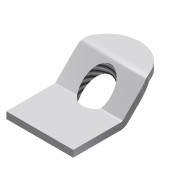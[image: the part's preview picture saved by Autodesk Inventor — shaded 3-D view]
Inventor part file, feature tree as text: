
AUTODESK INVENTOR PART (.ipt)
format: ipt  version: 2015 (Build 190159000, 159)  size: 161,792 bytes
history: native  units: mm
features: sketch x3, sweep x1, fillet x1, hole x1, pattern_linear x1, other x1
ambient origin geometry x8: Origin, YZ Plane, XZ Plane, XY Plane, X Axis, Y Axis, Z Axis, Center Point
bodies: Body1 (feature_tree)
feature tree (8):
  sweep  "Przeciągnięcie1"
  fillet  "Zaokrąglenie1"  Radius=20.594885mm
  hole  "Otwór1"  [1 undecoded]
  pattern_linear  "Szyk prostokątny2"  Spacing1=2.0mm  [1 undecoded]
  sketch  "Szkic1"
  sketch  "Szkic2"
  sketch  "Szkic5"
  other  "Bryła3"
note: 2 required parameter values undecoded (feature->parameter linkage not recoverable at this tier; creation-order binding heuristic only, values carry confidence <= 0.55)
